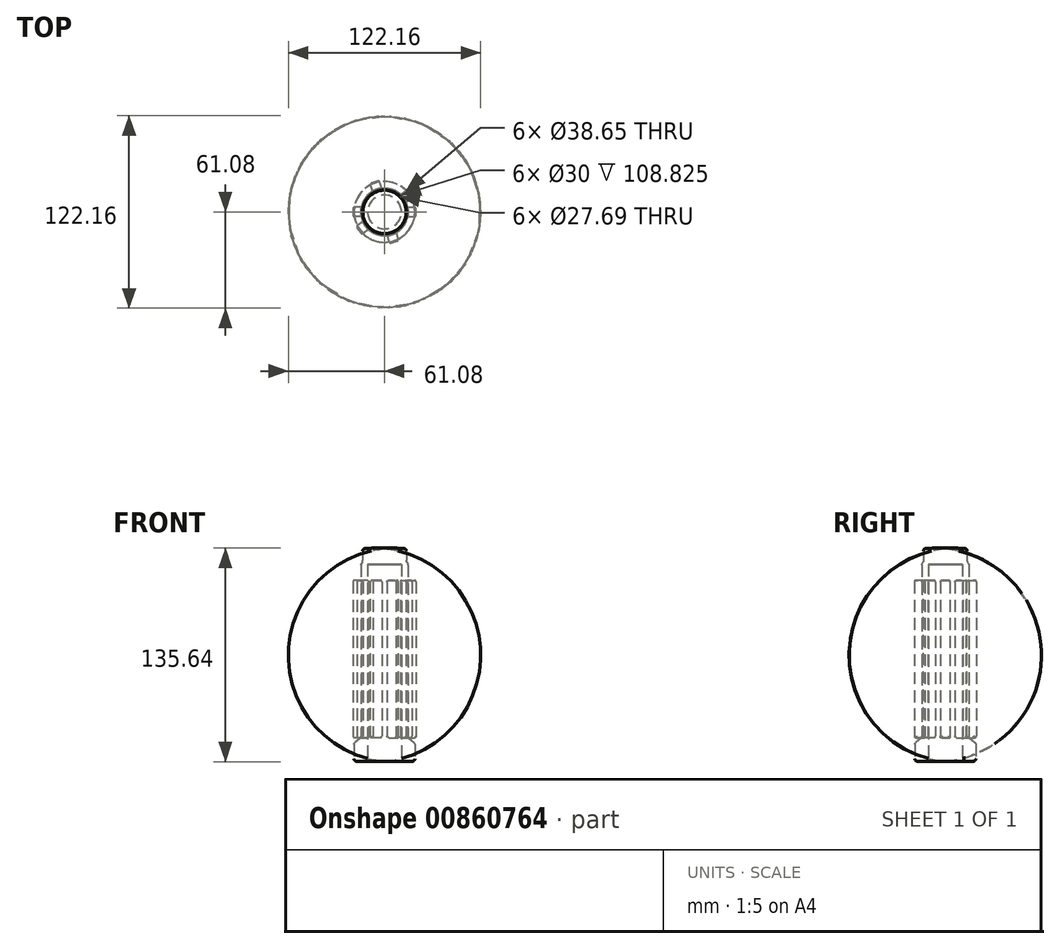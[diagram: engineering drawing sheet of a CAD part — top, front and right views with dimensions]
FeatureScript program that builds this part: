
annotation { "Feature Type Name" : "Feature", "Feature Type Description" : "" }
export const myFeature = defineFeature(function(context is Context, id is Id, definition is map)
    precondition{}
    {
        {
            var Q0;
            Q0=qCreatedBy(makeId("Front.planeOp"),FACE);
            var sketch = newSketch(context, id + "F0", { "sketchPlane" : qUnion([Q0])});
            skLineSegment(sketch, "E0", {"start": v(0, 0) * mm, "end": v(0, 125) * mm, "construction": true});
            skLineSegment(sketch, "E1", {"start": v(0, 135) * mm, "end": v(0, 125) * mm});
            skLineSegment(sketch, "E2", {"start": v(0, 125) * mm, "end": v(10.75, 125) * mm});
            skLineSegment(sketch, "E3", {"start": v(10.75, 125) * mm, "end": v(10.75, 0) * mm});
            skLineSegment(sketch, "E4", {"start": v(10.75, 0) * mm, "end": v(19.33, 0) * mm});
            skLineSegment(sketch, "E5", {"start": v(19.33, 0) * mm, "end": v(19.33, 11.37) * mm});
            skLineSegment(sketch, "E6", {"start": v(19.33, 11.37) * mm, "end": v(15, 15) * mm});
            skLineSegment(sketch, "E7", {"start": v(15, 15) * mm, "end": v(15, 125) * mm});
            skLineSegment(sketch, "E8", {"start": v(15, 125) * mm, "end": v(13.85, 127) * mm});
            skLineSegment(sketch, "E9", {"start": v(13.85, 127) * mm, "end": v(13.85, 135) * mm});
            skArc(sketch, "E10", {"start": v(13.85, 135) * mm, "mid": v(6.92, 135.35) * mm, "end": v(0, 135) * mm});
            skSolve(sketch);
        }
        {
            var Q0;
            Q0=qSketchRegion(id+"F0",true);
            var Q1;
            Q1=sQuery(id+"F0.wireOp",EDGE,"E0");
            revolve(context, id + "F1", {"surfaceOperationType" : NewSurfaceOperationType.NEW, "entities" : qUnion([Q0]), "axis" : qUnion([Q1]), "revolveType" : RevolveType.FULL});
        }
        {
            var Q0;
            Q0=makeQuery(id+"F1.opRevolve","SWEPT_EDGE",EDGE,{"disambiguationData":[OSD([sQuery(id+"F0.wireOp",EDGE,"E9"),sQuery(id+"F0.wireOp",EDGE,"E10")])]});
            var Q1;
            Q1=makeQuery(id+"F1.opRevolve","SWEPT_EDGE",EDGE,{"disambiguationData":[OSD([sQuery(id+"F0.wireOp",EDGE,"E8"),sQuery(id+"F0.wireOp",EDGE,"E9")])]});
            var Q2;
            Q2=makeQuery(id+"F1.opRevolve","SWEPT_EDGE",EDGE,{"disambiguationData":[OSD([sQuery(id+"F0.wireOp",EDGE,"E7"),sQuery(id+"F0.wireOp",EDGE,"E8")])]});
            var Q3;
            Q3=makeQuery(id+"F1.opRevolve","SWEPT_EDGE",EDGE,{"disambiguationData":[OSD([sQuery(id+"F0.wireOp",EDGE,"E6"),sQuery(id+"F0.wireOp",EDGE,"E7")])]});
            var Q4;
            Q4=makeQuery(id+"F1.opRevolve","SWEPT_EDGE",EDGE,{"disambiguationData":[OSD([sQuery(id+"F0.wireOp",EDGE,"E5"),sQuery(id+"F0.wireOp",EDGE,"E6")])]});
            var Q5;
            Q5=makeQuery(id+"F1.opRevolve","SWEPT_EDGE",EDGE,{"disambiguationData":[OSD([sQuery(id+"F0.wireOp",EDGE,"E4"),sQuery(id+"F0.wireOp",EDGE,"E5")])]});
            fillet(context, id + "F2", {"entities" : qUnion([Q0, Q1, Q2, Q3, Q4, Q5]), "radius" : 1.6 * mm, "tangentPropagation" : true, "allowEdgeOverflow" : false});
        }
        {
            var Q0;
            Q0=qCreatedBy(makeId("Right.planeOp"),FACE);
            cPlane(context, id + "F3", {"entities" : qUnion([Q0]), "cplaneType" : CPlaneType.OFFSET, "offset" : 20 * mm, "width" : 150 * mm, "height" : 150 * mm});
        }
        {
            var Q0;
            Q0=qCreatedBy(id+"F3.planeOp",FACE);
            var sketch = newSketch(context, id + "F4", { "sketchPlane" : qUnion([Q0])});
            skLineSegment(sketch, "E11.bottom", {"start": v(-3, 115) * mm, "end": v(3, 115) * mm});
            skLineSegment(sketch, "E11.top", {"start": v(-3, 15) * mm, "end": v(3, 15) * mm});
            skLineSegment(sketch, "E11.left", {"start": v(-3, 115) * mm, "end": v(-3, 15) * mm});
            skLineSegment(sketch, "E11.right", {"start": v(3, 115) * mm, "end": v(3, 15) * mm});
            skSolve(sketch);
        }
        {
            var Q0;
            Q0=qSketchRegion(id+"F4",true);
            var Q1;
            Q1=makeQuery(id+"F1.opRevolve","SWEPT_FACE",FACE,{"disambiguationData":[OSD([sQuery(id+"F0.wireOp",EDGE,"E7")])]});
            extrude(context, id + "F5", {"entities" : qUnion([Q0]), "operationType" : NewBodyOperationType.ADD, "endBound" : BoundingType.UP_TO_SURFACE, "oppositeDirection" : true, "depth" : 25 * mm, "endBoundEntityFace" : qUnion([Q1]), "offsetDistance" : 25 * mm});
        }
        {
            var Q0;
            Q0=makeQuery(id+"F5.opExtrude","CAP_EDGE",EDGE,{"disambiguationData":[OSD([sQuery(id+"F4.wireOp",EDGE,"E11.right")])],"isStart":true});
            var Q1;
            Q1=makeQuery(id+"F5.opExtrude","SWEPT_EDGE",EDGE,{"disambiguationData":[OSD([sQuery(id+"F4.wireOp",EDGE,"E11.bottom"),sQuery(id+"F4.wireOp",EDGE,"E11.right")])]});
            var Q2;
            Q2=makeQuery(id+"F5.opExtrude","SWEPT_EDGE",EDGE,{"disambiguationData":[OSD([sQuery(id+"F4.wireOp",EDGE,"E11.bottom"),sQuery(id+"F4.wireOp",EDGE,"E11.left")])]});
            var Q3;
            Q3=makeQuery(id+"F5.opExtrude","CAP_EDGE",EDGE,{"disambiguationData":[OSD([sQuery(id+"F4.wireOp",EDGE,"E11.left")])],"isStart":true});
            var Q4;
            Q4=makeQuery(id+"F5.opExtrude","CAP_EDGE",EDGE,{"disambiguationData":[OSD([sQuery(id+"F4.wireOp",EDGE,"E11.bottom")])],"isStart":true});
            var Q5;
            Q5=makeQuery(id+"F5.opExtrude","CAP_EDGE",EDGE,{"disambiguationData":[OSD([sQuery(id+"F4.wireOp",EDGE,"E11.top")])],"isStart":true});
            var Q6;
            Q6=makeQuery(id+"F5.opExtrude","SWEPT_EDGE",EDGE,{"disambiguationData":[OSD([sQuery(id+"F4.wireOp",EDGE,"E11.top"),sQuery(id+"F4.wireOp",EDGE,"E11.left")])]});
            fillet(context, id + "F6", {"entities" : qUnion([Q0, Q1, Q2, Q3, Q4, Q5, Q6]), "radius" : 1 * mm, "allowEdgeOverflow" : false});
        }
        {
            var Q0;
            Q0=makeQuery(id+"F1.opRevolve","SWEPT_BODY",BODY,{"disambiguationData":[OSD([sQuery(id+"F0.wireOp",EDGE,"E1"),sQuery(id+"F0.wireOp",EDGE,"E2"),sQuery(id+"F0.wireOp",EDGE,"E3"),sQuery(id+"F0.wireOp",EDGE,"E4"),sQuery(id+"F0.wireOp",EDGE,"E5"),sQuery(id+"F0.wireOp",EDGE,"E6"),sQuery(id+"F0.wireOp",EDGE,"E7"),sQuery(id+"F0.wireOp",EDGE,"E8"),sQuery(id+"F0.wireOp",EDGE,"E9"),sQuery(id+"F0.wireOp",EDGE,"E10")])]});
            var Q1;
            Q1=sQuery(id+"F0.wireOp",EDGE,"E0");
            circularPattern(context, id + "F7", {"entities" : qUnion([Q0]), "axis" : qUnion([Q1]), "angle" : 360 * degree, "instanceCount" : 10, "equalSpace" : true});
        }
    });
